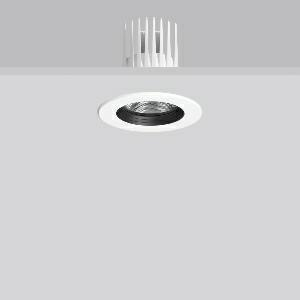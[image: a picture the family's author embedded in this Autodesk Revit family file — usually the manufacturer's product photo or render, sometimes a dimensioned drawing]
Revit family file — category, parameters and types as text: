
# Revit family: heledon_mini_e_901748_002_2_76_ec46
name_source: partatom
category: Lighting Fixtures
units: mm (PartAtom-declared; Revit-internal decimal feet)

## family parameters
Cut with Voids When Loaded = No
Host = Face
Light Source = No
Part Type = Normal
Room Calculation Point = No
Round Connector Dimension = Use Diameter
Shared = No

## types (1)
- HELEDON mini E (1 x LED Modul 927, 3400 lm, 2700)
    Apparent Load = 29 VA
    Approval mark = CE
    CIE Flux Codes = 100 100 100 100 100
    Color Rendering = 92
    Color Temperature = 2700
    Default Elevation = 1800 mm
    Description = Series: HELEDON mini
Round recessed downlight. Housing: die-cast aluminium, powder-coated. Black plastic ring and recessed LED to prevent glare from the side. Optical assembly with reflector made of MIRO-Silver with 98% total light reflection for outstanding efficiency - can be changed without tools. Best colour rendering index Ra>90. Suitable for Recessed ceiling mounting. Installation without tools thanks to spring fastening system. Including separate LED converter with connecting cable 600 mm.High quality converter without flickering and stroboscopic effect. Through-wiring box (5 pole) available as accessory. The following accessories can be mounted without use of tools: interchangeable lenses, decorative glasses, honeycomb louvre, clear and frosted diffusers, white interchangeable plastic ring. 
Colour: traffic white, matt (RAL 9016)
Diameter: 124 mm
Height: 3 mm
Cut-out diameter: 114 mm
Recess height: 170 mm
Luminaire: recess height: 120 mm
Lamp: LED
Socket: without socket
Colour temperature: 2700K
Colour rendering index (CRI): 92
System power: 29 W
Rated luminous flux: 3400 lm
Luminous efficiency: 117 lm/W
Control gear: Converter, dimmable, DALI
Protection class: II
Type of protection: IP 20
    Height = 0 mm  [stored 0 ft]
    Lamp = 1 x LED Modul 927
    Lamp Light Flux = 3400 lm
    Lamp count = 1
    Length = 124 mm  [stored 0.406824 ft]
    Lifetime = 50000 h
    Luminous efficacy = 117 lm/W
    Manufacturer = RZB
    ModVariant = No
    Model = 901748.002.2.76
    Mounting Place = Ceiling
    Mounting Type = Recessed
    Number of Poles = 1
    OnlyDefault = Yes
    Power Factor = 1
    Product Name = HELEDON mini E
    Product group = Recessed downlights
    ProductGroupID = 402
    Protection Class = Protection class II
    Protection Degree = IP 20
    RLX_Detail_Level = 1
    RLX_Emergency_Light_Flux = 0 lm
    RLX_Emergency_Type = 0
    RLX_Emergency_Type_DB = No
    RlxData = <blob elided: 127301 chars, md5=1ba2d361>
    Socket = socket
    Standby Power = 0 W
    System Light Flux = 3400 lm
    System Power = 29 W
    Type Comments = Product without accessories
    Type Image = 901657.002.jpg
    URL = http://relux.com
    VarID = ---
    Voltage = 230 V
    Voltage Range = 220-240 V
    Weight = 0.00 kg
    Width = 0 mm  [stored 0 ft]

note: [stored X ft] marks values corroborated as IEEE doubles in the binary element streams (Revit-internal decimal feet)

## geometry (parser evidence)
native form markers: Blend x4, Sweep x12
no freeform markers — native parametric forms only
